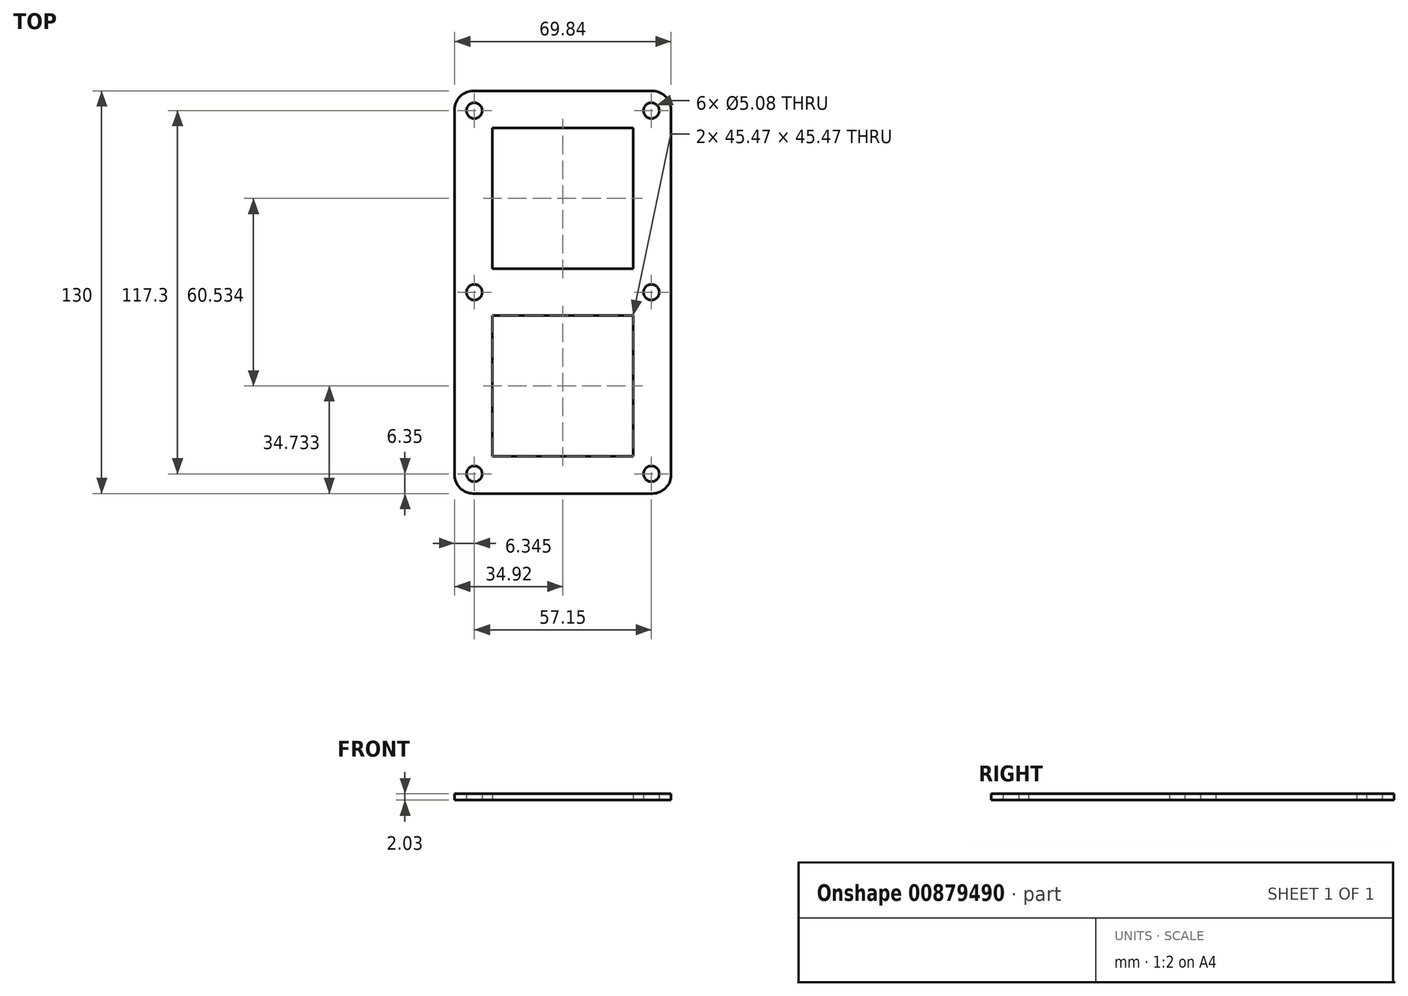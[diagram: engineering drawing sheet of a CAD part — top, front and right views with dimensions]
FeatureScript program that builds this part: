
annotation { "Feature Type Name" : "Feature", "Feature Type Description" : "" }
export const myFeature = defineFeature(function(context is Context, id is Id, definition is map)
    precondition{}
    {
        {
            var Q0;
            Q0=qCreatedBy(makeId("Top.planeOp"),FACE);
            var sketch = newSketch(context, id + "F0", { "sketchPlane" : qUnion([Q0])});
            skLineSegment(sketch, "E0.bottom", {"start": v(-28.93, 65) * mm, "end": v(28.93, 65) * mm});
            skLineSegment(sketch, "E0.top", {"start": v(-28.93, -65) * mm, "end": v(28.93, -65) * mm});
            skLineSegment(sketch, "E0.left", {"start": v(-34.93, 59) * mm, "end": v(-34.93, -59) * mm});
            skLineSegment(sketch, "E0.right", {"start": v(34.93, 59) * mm, "end": v(34.93, -59) * mm});
            skCircle(sketch, "E1", {"center": v(-28.57, 58.65) * mm, "radius": 2.54 * mm});
            skCircle(sketch, "E2.1.0.0", {"center": v(28.57, 58.65) * mm, "radius": 2.54 * mm});
            skLineSegment(sketch, "E2.direction1", {"start": v(-28.57, 58.65) * mm, "end": v(28.57, 58.65) * mm, "construction": true});
            skCircle(sketch, "E3.MirrorC", {"center": v(-28.57, -58.65) * mm, "radius": 2.54 * mm});
            skCircle(sketch, "E4.MirrorC", {"center": v(28.57, -58.65) * mm, "radius": 2.54 * mm});
            skCircle(sketch, "E5", {"center": v(-28.58, 0) * mm, "radius": 2.54 * mm});
            skCircle(sketch, "E6.MirrorC", {"center": v(28.58, 0) * mm, "radius": 2.54 * mm});
            skLineSegment(sketch, "E7.bottom", {"start": v(-22.73, 53) * mm, "end": v(22.73, 53) * mm});
            skLineSegment(sketch, "E7.top", {"start": v(-22.73, 7.53) * mm, "end": v(22.73, 7.53) * mm});
            skLineSegment(sketch, "E7.left", {"start": v(-22.73, 53) * mm, "end": v(-22.73, 7.53) * mm});
            skLineSegment(sketch, "E7.right", {"start": v(22.73, 53) * mm, "end": v(22.73, 7.53) * mm});
            skLineSegment(sketch, "E8.MirrorCS", {"start": v(22.73, -53) * mm, "end": v(22.73, -7.53) * mm});
            skLineSegment(sketch, "E9.MirrorCS", {"start": v(-22.73, -53) * mm, "end": v(-22.73, -7.53) * mm});
            skLineSegment(sketch, "E10.MirrorCS", {"start": v(-22.73, -53) * mm, "end": v(22.73, -53) * mm});
            skLineSegment(sketch, "E11.MirrorCS", {"start": v(-22.73, -7.53) * mm, "end": v(22.73, -7.53) * mm});
            skPoint(sketch, "E12.visualSharp", {"position": v(-34.93, 65) * mm});
            skArc(sketch, "E12.filletArc", {"start": v(-28.93, 65) * mm, "mid": v(-33.17, 63.24) * mm, "end": v(-34.93, 59) * mm});
            skPoint(sketch, "E13.visualSharp", {"position": v(34.93, 65) * mm});
            skArc(sketch, "E13.filletArc", {"start": v(34.93, 59) * mm, "mid": v(33.17, 63.24) * mm, "end": v(28.93, 65) * mm});
            skPoint(sketch, "E14.visualSharp", {"position": v(34.93, -65) * mm});
            skArc(sketch, "E14.filletArc", {"start": v(28.93, -65) * mm, "mid": v(33.17, -63.24) * mm, "end": v(34.93, -59) * mm});
            skPoint(sketch, "E15.visualSharp", {"position": v(-34.93, -65) * mm});
            skArc(sketch, "E15.filletArc", {"start": v(-34.93, -59) * mm, "mid": v(-33.17, -63.24) * mm, "end": v(-28.93, -65) * mm});
            skSolve(sketch);
        }
        {
            var Q0;
            Q0=makeQuery(id+"F0.imprint","IMPRINT",FACE,{"disambiguationData":[TD([[makeQuery(id+"F0.imprint","IMPRINT",EDGE,{"derivedFrom":sQuery(id+"F0.wireOp",EDGE,"E0.bottom")}),-1.0]])]});
            extrude(context, id + "F1", {"entities" : qUnion([Q0]), "depth" : 2.03 * mm, "offsetDistance" : 25.4 * mm});
        }
    });
